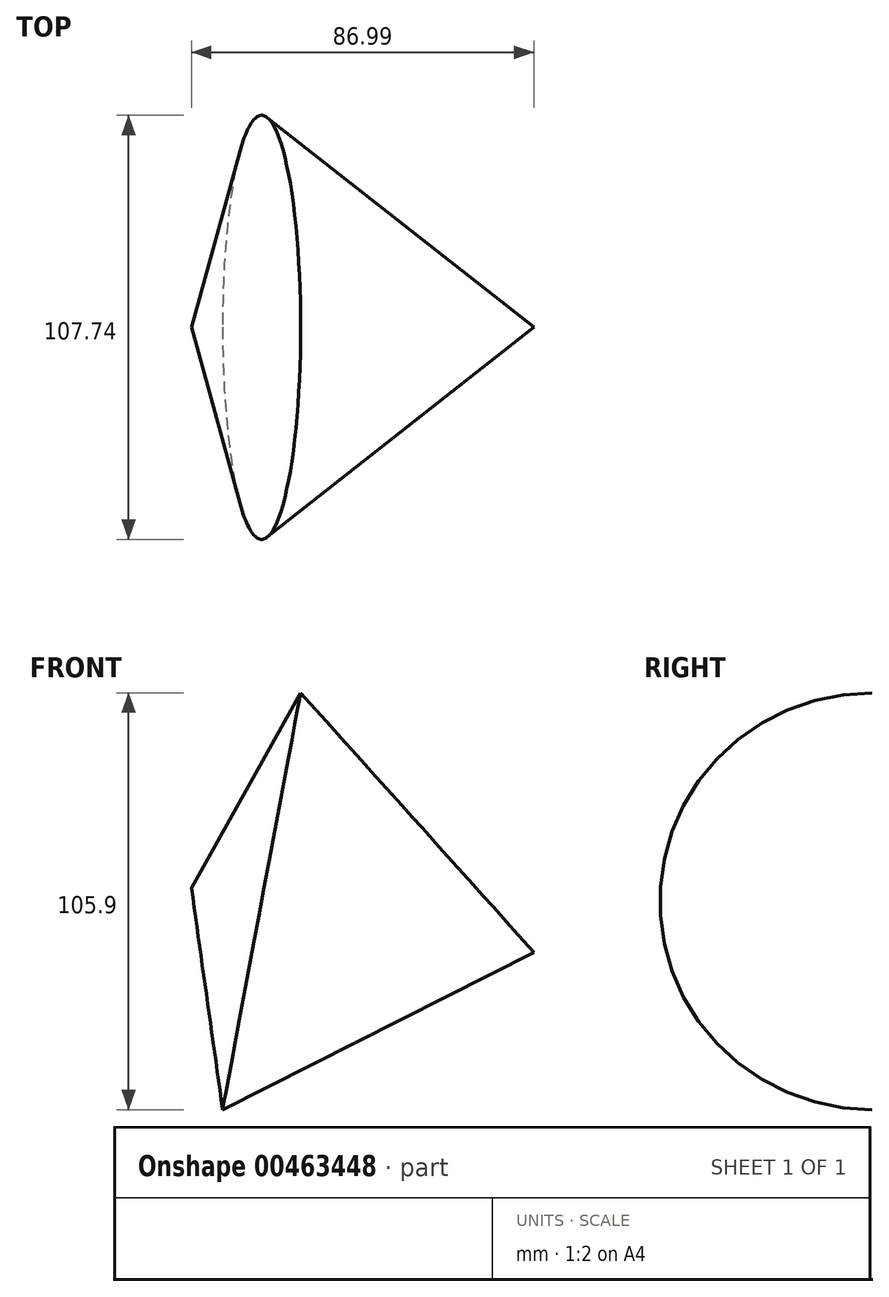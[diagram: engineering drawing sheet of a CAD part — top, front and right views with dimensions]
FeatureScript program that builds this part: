
annotation { "Feature Type Name" : "Feature", "Feature Type Description" : "" }
export const myFeature = defineFeature(function(context is Context, id is Id, definition is map)
    precondition{}
    {
        {
            var Q0;
            Q0=qCreatedBy(makeId("Front.planeOp"),FACE);
            var sketch = newSketch(context, id + "F0", { "sketchPlane" : qUnion([Q0])});
            skLineSegment(sketch, "E0", {"start": v(-46.05, 44.2) * mm, "end": v(40.94, 27.91) * mm});
            skLineSegment(sketch, "E1", {"start": v(40.94, 27.91) * mm, "end": v(-38.14, -12.1) * mm});
            skLineSegment(sketch, "E2", {"start": v(-38.14, -12.1) * mm, "end": v(-46.05, 44.2) * mm});
            skSolve(sketch);
        }
        {
            var Q0;
            Q0 = qSketchRegion(id + "F0", true);
            var Q1;
            Q1=makeQuery(id+"F0.imprint","IMPRINT",FACE,{"disambiguationData":[TD([[makeQuery(id+"F0.imprint","IMPRINT",EDGE,{"derivedFrom":sQuery(id+"F0.wireOp",EDGE,"E0")}),-1.0]])]});
            var Q2;
            Q2=sQuery(id+"F0.wireOp",EDGE,"E0");
            revolve(context, id + "F1", {"entities" : qUnion([Q0, Q1]), "axis" : qUnion([Q2]), "revolveType" : RevolveType.FULL});
        }
    });
